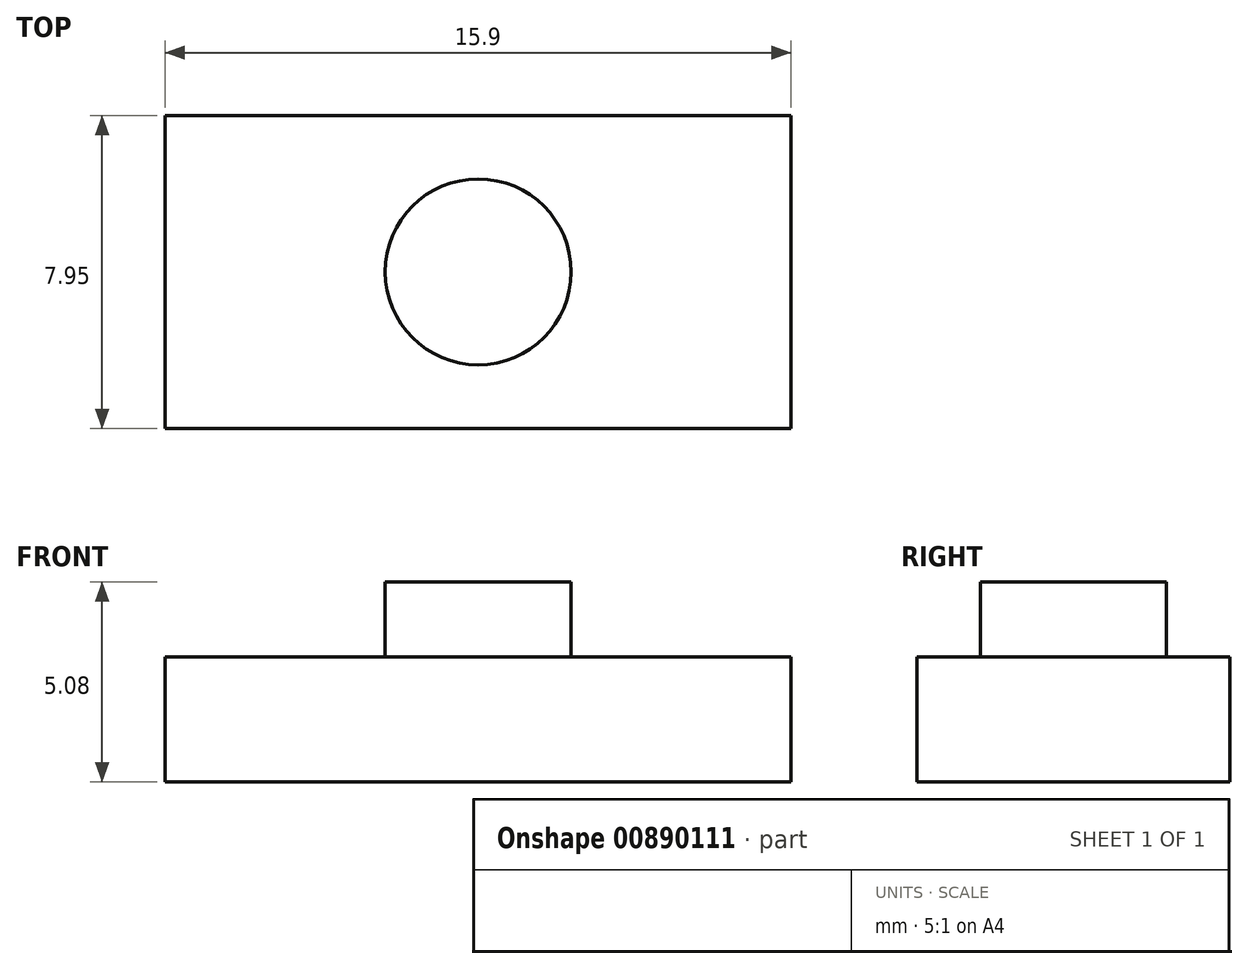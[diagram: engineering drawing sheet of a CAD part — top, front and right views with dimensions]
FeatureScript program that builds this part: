
annotation { "Feature Type Name" : "Feature", "Feature Type Description" : "" }
export const myFeature = defineFeature(function(context is Context, id is Id, definition is map)
    precondition{}
    {
        {
            var Q0;
            Q0=qCreatedBy(makeId("Top.planeOp"),FACE);
            var sketch = newSketch(context, id + "F0", { "sketchPlane" : qUnion([Q0])});
            skLineSegment(sketch, "E0.bottom", {"start": v(-9.05, 13.27) * mm, "end": v(6.85, 13.27) * mm});
            skLineSegment(sketch, "E0.top", {"start": v(-9.05, 5.32) * mm, "end": v(6.85, 5.32) * mm});
            skLineSegment(sketch, "E0.left", {"start": v(-9.05, 13.27) * mm, "end": v(-9.05, 5.32) * mm});
            skLineSegment(sketch, "E0.right", {"start": v(6.85, 13.27) * mm, "end": v(6.85, 5.32) * mm});
            skLineSegment(sketch, "E1", {"start": v(-9.05, 13.27) * mm, "end": v(6.85, 5.32) * mm});
            skCircle(sketch, "E2", {"center": v(-1.1, 9.3) * mm, "radius": 2.36 * mm});
            skSolve(sketch);
        }
        {
            var Q0;
            {var subQ4=sQuery(id+"F0.wireOp",EDGE,"E0.bottom");Q0=makeQuery(id+"F0.imprint","IMPRINT",FACE,{"disambiguationData":[TD([[makeQuery(id+"F0.imprint","IMPRINT",EDGE,{"derivedFrom":subQ4}),-1.0]])]});}
            var Q1;
            {var subQ4=sQuery(id+"F0.wireOp",EDGE,"E0.top");Q1=makeQuery(id+"F0.imprint","IMPRINT",FACE,{"disambiguationData":[TD([[makeQuery(id+"F0.imprint","IMPRINT",EDGE,{"derivedFrom":subQ4}),1.0]])]});}
            var Q2;
            {var subQ0=sQuery(id+"F0.wireOp",EDGE,"E2");var subQ1=sQuery(id+"F0.wireOp",EDGE,"E1");var subQ2=makeQuery(id+"F0.imprint","INTERSECT",VERTEX,{"disambiguationData":[OD(0.0)],"derivedFrom":[subQ1,subQ0]});Q2=makeQuery(id+"F0.imprint","IMPRINT",FACE,{"disambiguationData":[TD([[makeQuery(id+"F0.imprint","IMPRINT",EDGE,{"disambiguationData":[TD([[subQ2,-1.0]])],"derivedFrom":subQ1}),1.0]])]});}
            var Q3;
            {var subQ0=sQuery(id+"F0.wireOp",EDGE,"E2");var subQ1=sQuery(id+"F0.wireOp",EDGE,"E1");var subQ2=makeQuery(id+"F0.imprint","INTERSECT",VERTEX,{"disambiguationData":[OD(0.0)],"derivedFrom":[subQ1,subQ0]});Q3=makeQuery(id+"F0.imprint","IMPRINT",FACE,{"disambiguationData":[TD([[makeQuery(id+"F0.imprint","IMPRINT",EDGE,{"disambiguationData":[TD([[subQ2,-1.0]])],"derivedFrom":subQ1}),-1.0]])]});}
            extrude(context, id + "F1", {"entities" : qUnion([Q0, Q1, Q2, Q3]), "depth" : 3.17 * mm, "offsetDistance" : 25.4 * mm});
        }
        {
            var Q0;
            {var subQ0=sQuery(id+"F0.wireOp",EDGE,"E2");var subQ1=sQuery(id+"F0.wireOp",EDGE,"E1");var subQ2=makeQuery(id+"F0.imprint","INTERSECT",VERTEX,{"disambiguationData":[OD(0.0)],"derivedFrom":[subQ1,subQ0]});Q0=makeQuery(id+"F0.imprint","IMPRINT",FACE,{"disambiguationData":[TD([[makeQuery(id+"F0.imprint","IMPRINT",EDGE,{"disambiguationData":[TD([[subQ2,-1.0]])],"derivedFrom":subQ1}),1.0]])]});}
            var Q1;
            {var subQ0=sQuery(id+"F0.wireOp",EDGE,"E2");var subQ1=sQuery(id+"F0.wireOp",EDGE,"E1");var subQ2=makeQuery(id+"F0.imprint","INTERSECT",VERTEX,{"disambiguationData":[OD(0.0)],"derivedFrom":[subQ1,subQ0]});Q1=makeQuery(id+"F0.imprint","IMPRINT",FACE,{"disambiguationData":[TD([[makeQuery(id+"F0.imprint","IMPRINT",EDGE,{"disambiguationData":[TD([[subQ2,-1.0]])],"derivedFrom":subQ1}),-1.0]])]});}
            extrude(context, id + "F2", {"entities" : qUnion([Q0, Q1]), "operationType" : NewBodyOperationType.ADD, "depth" : 5.08 * mm, "offsetDistance" : 25.4 * mm});
        }
    });
